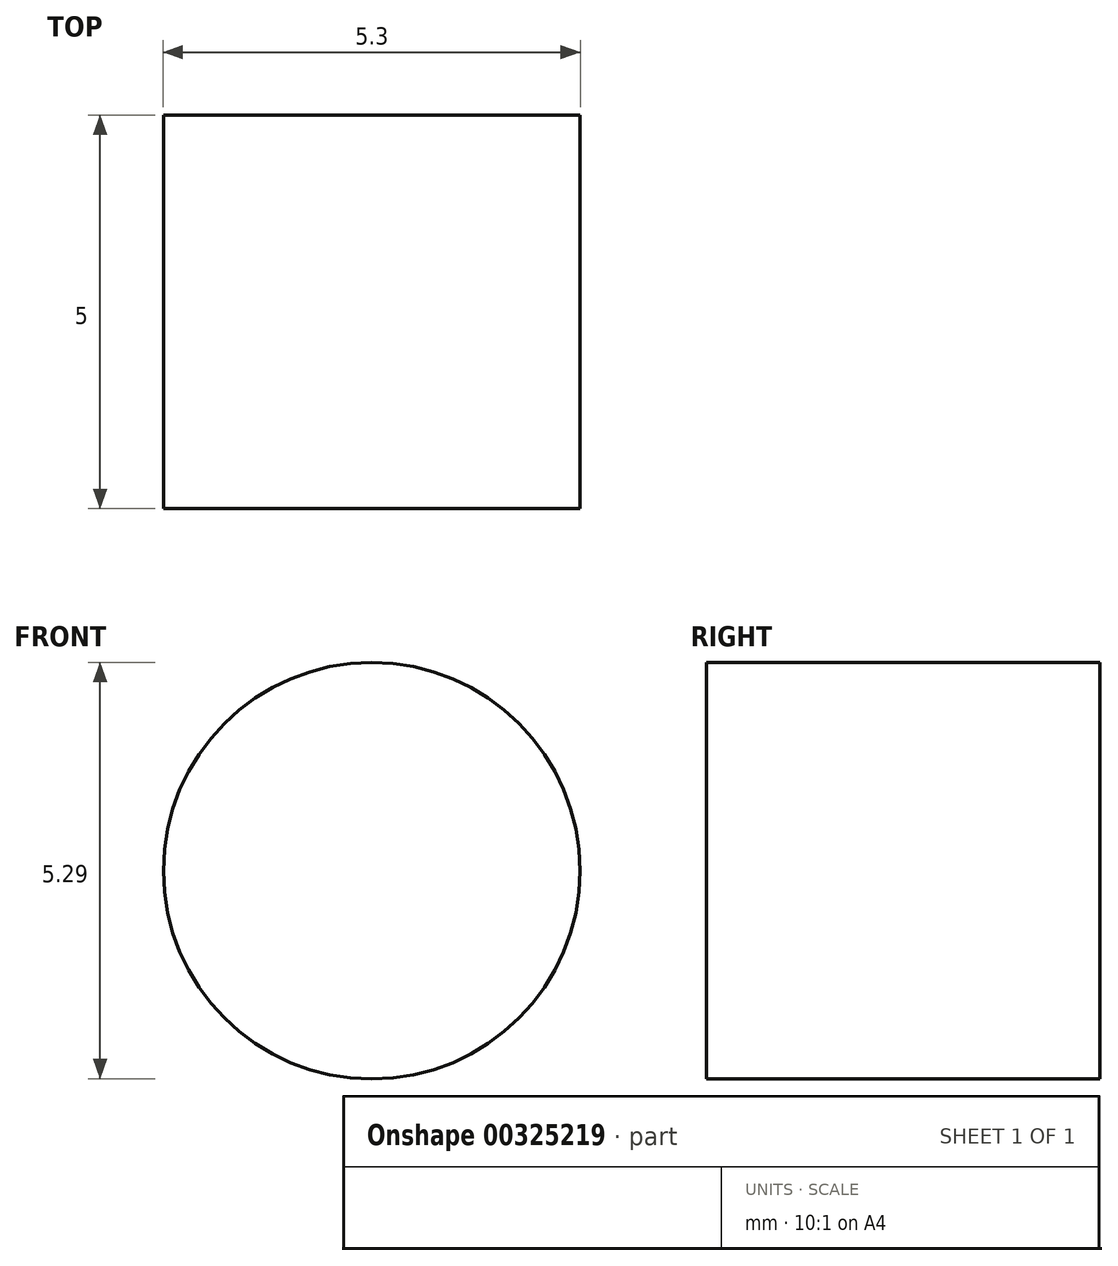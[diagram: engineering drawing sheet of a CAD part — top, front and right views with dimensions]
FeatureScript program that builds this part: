
annotation { "Feature Type Name" : "Feature", "Feature Type Description" : "" }
export const myFeature = defineFeature(function(context is Context, id is Id, definition is map)
    precondition{}
    {
        {
            var Q0;
            Q0=qCreatedBy(makeId("Front.planeOp"),FACE);
            var sketch = newSketch(context, id + "F0", { "sketchPlane" : qUnion([Q0])});
            skEllipse(sketch, "E0", {"center": v(18.79, 36.14) * mm, "majorRadius": 59.42 * mm, "minorRadius": 28.97 * mm, "majorAxis": v(0, -1)});
            skSolve(sketch);
        }
        {
            var Q0;
            Q0 = qSketchRegion(id + "F2", true);
            var Q1;
            Q1=makeQuery(id+"F0.imprint","IMPRINT",FACE,{"disambiguationData":[TD([[makeQuery(id+"F0.imprint","IMPRINT",EDGE,{"derivedFrom":sQuery(id+"F0.wireOp",EDGE,"E0")}),1.0]])]});
            extrude(context, id + "F1", {"entities" : qUnion([Q0, Q1]), "depth" : 5 * mm});
        }
        {
            var Q0;
            Q0=makeQuery(id+"F0.imprint","IMPRINT",FACE,{"disambiguationData":[TD([[makeQuery(id+"F0.imprint","IMPRINT",EDGE,{"derivedFrom":sQuery(id+"F0.wireOp",EDGE,"E0")}),1.0]])]});
            var sketch = newSketch(context, id + "F2", { "sketchPlane" : qUnion([Q0])});
            skCircle(sketch, "E1", {"center": v(19.34, 86.04) * mm, "radius": 2.65 * mm});
            skLineSegment(sketch, "E2", {"start": v(19.34, 35.66) * mm, "end": v(-31.98, 35.66) * mm, "construction": true});
            skLineSegment(sketch, "E3", {"start": v(-31.98, 35.66) * mm, "end": v(63.74, 35.66) * mm, "construction": true});
            skLineSegment(sketch, "E4", {"start": v(19.34, 35.66) * mm, "end": v(19.34, 98.46) * mm, "construction": true});
            skLineSegment(sketch, "E5", {"start": v(19.34, 98.46) * mm, "end": v(19.34, -27.37) * mm, "construction": true});
            skCircle(sketch, "E6.MirrorC", {"center": v(19.34, -14.72) * mm, "radius": 2.65 * mm});
            skSolve(sketch);
        }
        {
            var Q0;
            Q0=makeQuery(id+"F2.imprint","IMPRINT",FACE,{"disambiguationData":[TD([[makeQuery(id+"F2.imprint","IMPRINT",EDGE,{"derivedFrom":sQuery(id+"F2.wireOp",EDGE,"E1")}),1.0]])]});
            var Q1;
            Q1=makeQuery(id+"F2.imprint","IMPRINT",FACE,{"disambiguationData":[TD([[makeQuery(id+"F2.imprint","IMPRINT",EDGE,{"derivedFrom":sQuery(id+"F2.wireOp",EDGE,"E6.MirrorC")}),-1.0]])]});
            extrude(context, id + "F3", {"entities" : qUnion([Q0, Q1]), "operationType" : NewBodyOperationType.REMOVE, "depth" : 25 * mm});
        }
    });
